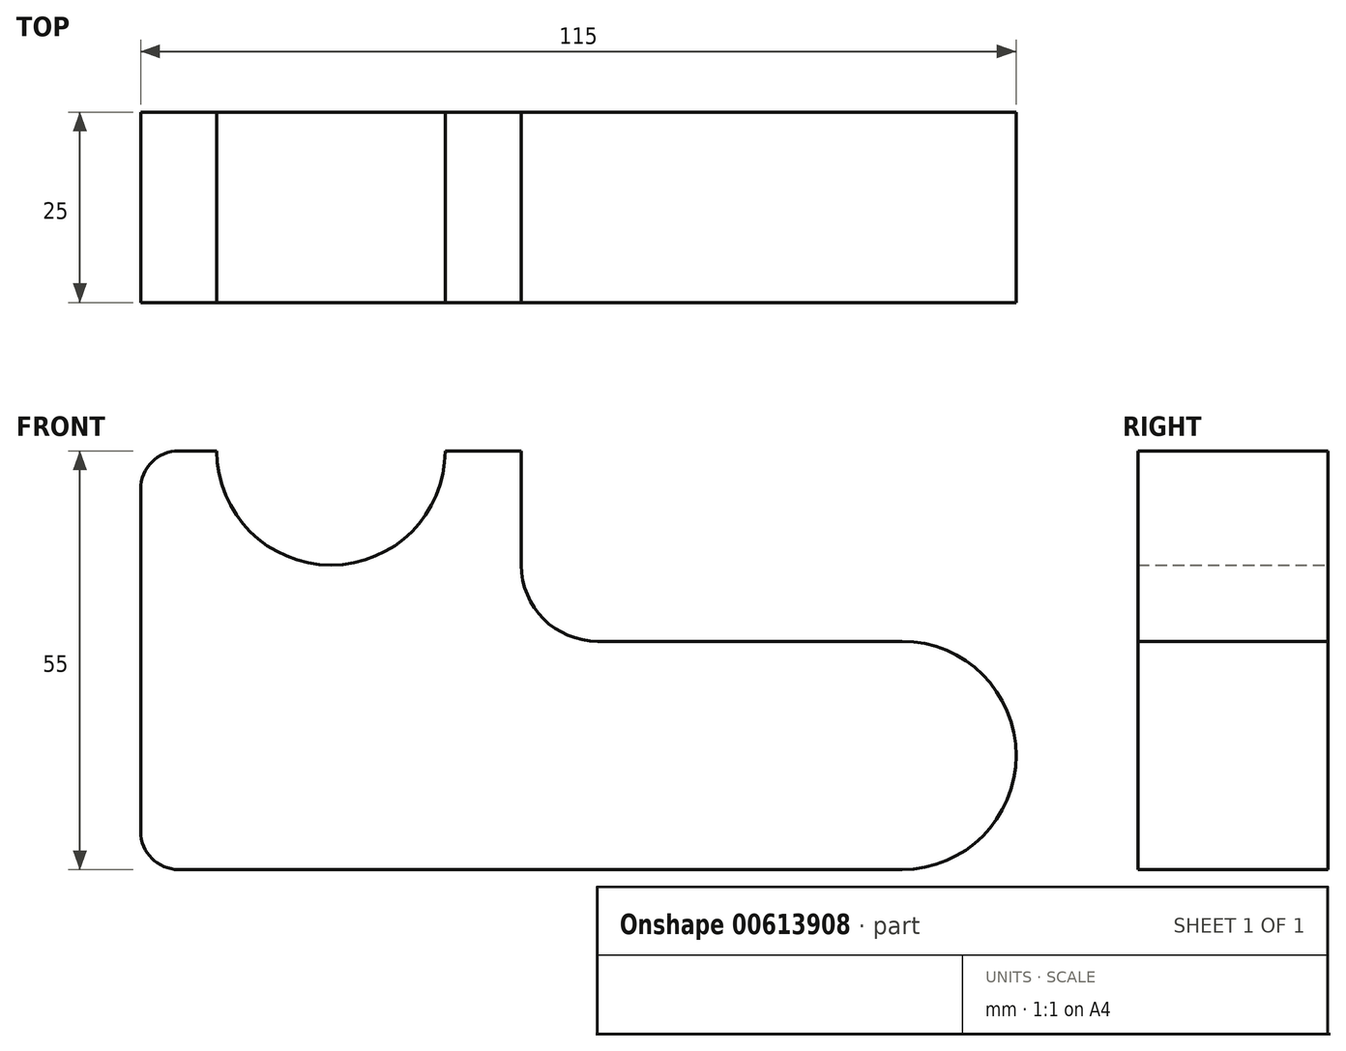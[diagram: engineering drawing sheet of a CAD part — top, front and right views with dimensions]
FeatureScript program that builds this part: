
annotation { "Feature Type Name" : "Feature", "Feature Type Description" : "" }
export const myFeature = defineFeature(function(context is Context, id is Id, definition is map)
    precondition{}
    {
        {
            var Q0;
            Q0=qCreatedBy(makeId("Front.planeOp"),FACE);
            var sketch = newSketch(context, id + "F0", { "sketchPlane" : qUnion([Q0])});
            skLineSegment(sketch, "E0", {"start": v(-47.6, 27.15) * mm, "end": v(-47.6, -17.85) * mm});
            skLineSegment(sketch, "E1", {"start": v(-42.6, -22.85) * mm, "end": v(52.4, -22.85) * mm});
            skLineSegment(sketch, "E2", {"start": v(52.4, 7.15) * mm, "end": v(12.4, 7.15) * mm});
            skLineSegment(sketch, "E3", {"start": v(2.4, 17.15) * mm, "end": v(2.4, 32.15) * mm});
            skLineSegment(sketch, "E4", {"start": v(2.4, 32.15) * mm, "end": v(-7.6, 32.15) * mm});
            skPoint(sketch, "E5.visualSharp", {"position": v(-47.6, 32.15) * mm});
            skArc(sketch, "E5.filletArc", {"start": v(-42.6, 32.15) * mm, "mid": v(-46.13, 30.69) * mm, "end": v(-47.6, 27.15) * mm});
            skPoint(sketch, "E6.visualSharp", {"position": v(-47.6, -22.85) * mm});
            skArc(sketch, "E6.filletArc", {"start": v(-47.6, -17.85) * mm, "mid": v(-46.13, -21.38) * mm, "end": v(-42.6, -22.85) * mm});
            skArc(sketch, "E7", {"start": v(52.4, -22.85) * mm, "mid": v(67.4, -7.85) * mm, "end": v(52.4, 7.15) * mm});
            skPoint(sketch, "E8", {"position": v(-37.6, 32.15) * mm});
            skPoint(sketch, "E9", {"position": v(-7.6, 32.15) * mm});
            skArc(sketch, "E10", {"start": v(-37.6, 32.15) * mm, "mid": v(-22.6, 17.15) * mm, "end": v(-7.6, 32.15) * mm});
            skLineSegment(sketch, "E11", {"start": v(-37.6, 32.15) * mm, "end": v(-42.6, 32.15) * mm});
            skLineSegment(sketch, "E12", {"start": v(-7.6, 32.15) * mm, "end": v(2.4, 32.15) * mm});
            skPoint(sketch, "E13.visualSharp", {"position": v(2.4, 7.15) * mm});
            skArc(sketch, "E13.filletArc", {"start": v(2.4, 17.15) * mm, "mid": v(5.34, 10.08) * mm, "end": v(12.4, 7.15) * mm});
            skSolve(sketch);
        }
        {
            var Q0;
            Q0 = qSketchRegion(id + "F0", true);
            extrude(context, id + "F1", {"entities" : qUnion([Q0]), "depth" : 25 * mm, "offsetDistance" : 25 * mm});
        }
    });
